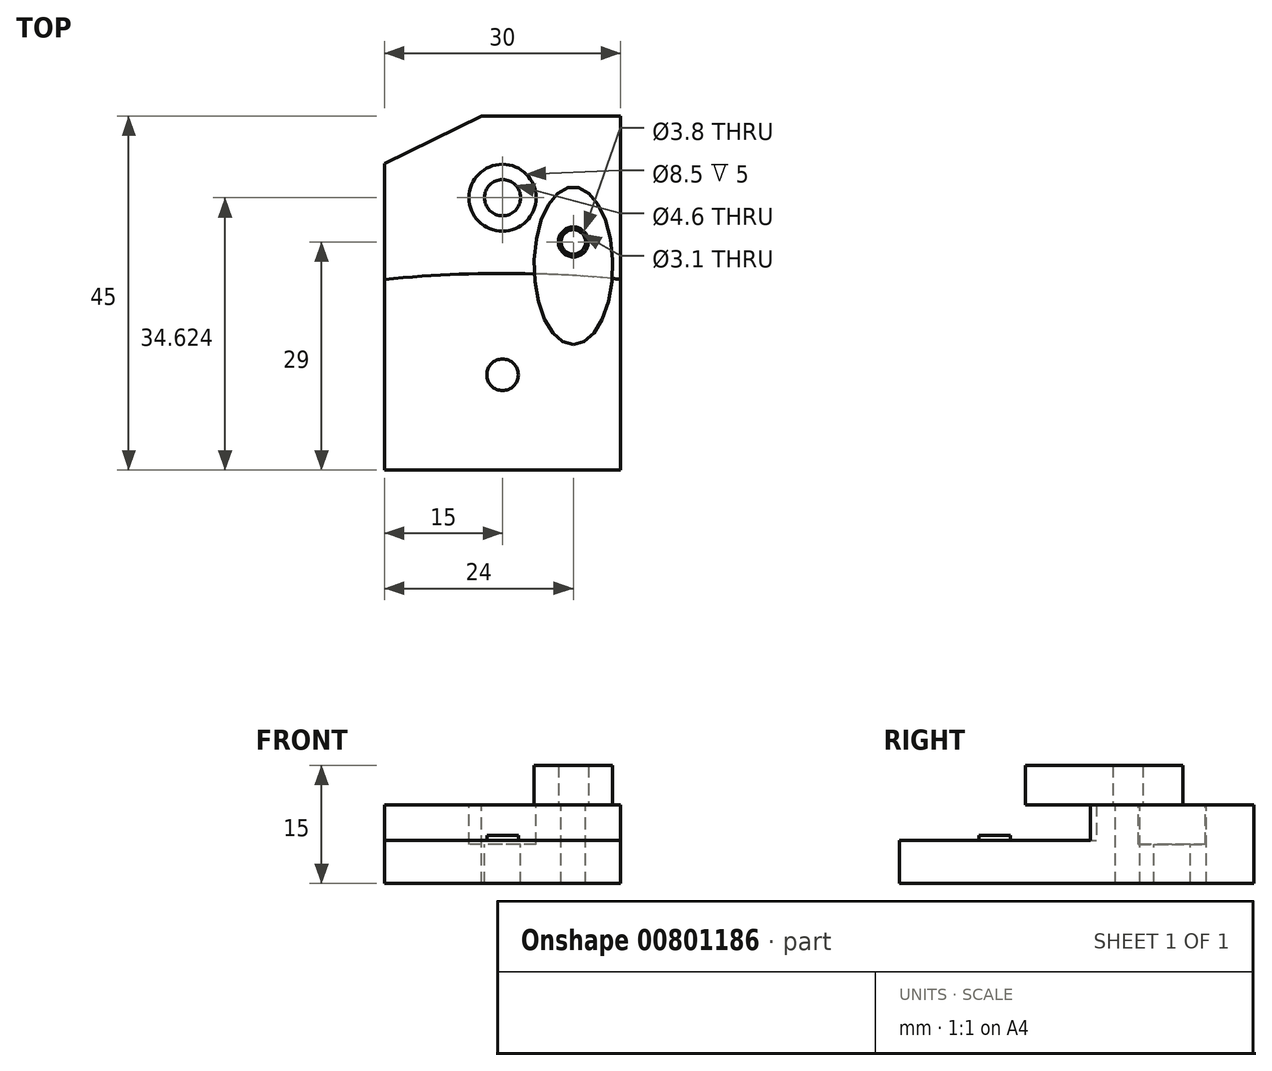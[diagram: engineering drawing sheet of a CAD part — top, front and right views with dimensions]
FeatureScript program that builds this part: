
annotation { "Feature Type Name" : "Feature", "Feature Type Description" : "" }
export const myFeature = defineFeature(function(context is Context, id is Id, definition is map)
    precondition{}
    {
        {
            var Q0;
            Q0=qCreatedBy(makeId("Top.planeOp"),FACE);
            var sketch = newSketch(context, id + "F0", { "sketchPlane" : qUnion([Q0])});
            skLineSegment(sketch, "E0.bottom", {"start": v(15, 22.5) * mm, "end": v(-15, 22.5) * mm});
            skLineSegment(sketch, "E0.top", {"start": v(15, -22.5) * mm, "end": v(-15, -22.5) * mm});
            skLineSegment(sketch, "E0.left", {"start": v(15, 22.5) * mm, "end": v(15, -22.5) * mm});
            skLineSegment(sketch, "E0.right", {"start": v(-15, 22.5) * mm, "end": v(-15, -22.5) * mm});
            skPoint(sketch, "E0.middle", {"position": v(0, 0) * mm});
            skLineSegment(sketch, "E1", {"start": v(15, 2.5) * mm, "end": v(-15, 2.5) * mm});
            skSolve(sketch);
        }
        {
            var Q0;
            {var subQ0=sQuery(id+"F0.wireOp",EDGE,"E0.top");Q0=makeQuery(id+"F0.imprint","IMPRINT",FACE,{"disambiguationData":[TD([[makeQuery(id+"F0.imprint","IMPRINT",EDGE,{"derivedFrom":subQ0}),-1.0]])]});}
            extrude(context, id + "F1", {"entities" : qUnion([Q0]), "oppositeDirection" : true, "depth" : 5.5 * mm, "offsetDistance" : 25 * mm});
        }
        {
            var Q0;
            {var subQ0=sQuery(id+"F0.wireOp",EDGE,"E0.bottom");Q0=makeQuery(id+"F0.imprint","IMPRINT",FACE,{"disambiguationData":[TD([[makeQuery(id+"F0.imprint","IMPRINT",EDGE,{"derivedFrom":subQ0}),1.0]])]});}
            extrude(context, id + "F2", {"entities" : qUnion([Q0]), "operationType" : NewBodyOperationType.ADD, "oppositeDirection" : true, "depth" : 5.5 * mm, "offsetDistance" : 25 * mm, "hasSecondDirection" : true, "secondDirectionOppositeDirection" : false, "secondDirectionDepth" : 4.5 * mm});
        }
        {
            var Q0;
            Q0=makeQuery(id+"F1.opExtrude","CAP_FACE",FACE,{"disambiguationData":[OSD([sQuery(id+"F0.wireOp",EDGE,"E0.top"),sQuery(id+"F0.wireOp",EDGE,"E0.left"),sQuery(id+"F0.wireOp",EDGE,"E0.right"),sQuery(id+"F0.wireOp",EDGE,"E1")])],"isStart":true});
            var sketch = newSketch(context, id + "F3", { "sketchPlane" : qUnion([Q0])});
            skLineSegment(sketch, "E2", {"start": v(0, 2.5) * mm, "end": v(0, -147.5) * mm, "construction": true});
            skCircle(sketch, "E3", {"center": v(0, -147.5) * mm, "radius": 150 * mm});
            skLineSegment(sketch, "E4", {"start": v(15, 2.6) * mm, "end": v(15, 1.75) * mm});
            skLineSegment(sketch, "E5", {"start": v(-15, 2.5) * mm, "end": v(-15, 1.75) * mm});
            skLineSegment(sketch, "E6", {"start": v(-15, 2.5) * mm, "end": v(15, 2.5) * mm});
            skSolve(sketch);
        }
        {
            var Q0;
            {var subQ0=sQuery(id+"F3.wireOp",EDGE,"E6");var subQ3=sQuery(id+"F3.wireOp",EDGE,"E4");var subQ5=makeQuery(id+"F3.imprint","INTERSECT",VERTEX,{"derivedFrom":[subQ3,subQ0]});Q0=makeQuery(id+"F3.imprint","IMPRINT",FACE,{"disambiguationData":[TD([[makeQuery(id+"F3.imprint","IMPRINT",EDGE,{"disambiguationData":[TD([[subQ5,-1.0]])],"derivedFrom":subQ0}),1.0]])]});}
            var Q1;
            {var subQ0=sQuery(id+"F3.wireOp",EDGE,"E5");Q1=makeQuery(id+"F3.imprint","IMPRINT",FACE,{"disambiguationData":[TD([[makeQuery(id+"F3.imprint","IMPRINT",EDGE,{"derivedFrom":subQ0}),1.0]])]});}
            var Q2;
            Q2=makeQuery(id+"F2.opExtrude","CAP_FACE",FACE,{"disambiguationData":[OSD([sQuery(id+"F0.wireOp",EDGE,"E0.bottom"),sQuery(id+"F0.wireOp",EDGE,"E0.left"),sQuery(id+"F0.wireOp",EDGE,"E0.right"),sQuery(id+"F0.wireOp",EDGE,"E1")])],"isStart":true});
            extrude(context, id + "F4", {"entities" : qUnion([Q0, Q1]), "operationType" : NewBodyOperationType.ADD, "endBound" : BoundingType.UP_TO_SURFACE, "depth" : 4 * mm, "endBoundEntityFace" : qUnion([Q2]), "offsetDistance" : 25 * mm});
        }
        {
            var Q0;
            Q0=makeQuery(id+"F1.opExtrude","CAP_FACE",FACE,{"disambiguationData":[OSD([sQuery(id+"F0.wireOp",EDGE,"E0.top"),sQuery(id+"F0.wireOp",EDGE,"E0.left"),sQuery(id+"F0.wireOp",EDGE,"E0.right"),sQuery(id+"F0.wireOp",EDGE,"E1")])],"isStart":true});
            var sketch = newSketch(context, id + "F5", { "sketchPlane" : qUnion([Q0])});
            skCircle(sketch, "E7", {"center": v(0, -10.38) * mm, "radius": 2 * mm});
            skPoint(sketch, "E7.centerSnap0", {"position": v(15, -10.38) * mm});
            skPoint(sketch, "E7.centerSnap1", {"position": v(0, -22.5) * mm});
            skSolve(sketch);
        }
        {
            var Q0;
            Q0 = qSketchRegion(id + "F5", true);
            extrude(context, id + "F6", {"entities" : qUnion([Q0]), "operationType" : NewBodyOperationType.ADD, "depth" : 0.6 * mm, "offsetDistance" : 25 * mm});
        }
        {
            var Q0;
            {var subQ0=sQuery(id+"F3.wireOp",EDGE,"E6");var subQ1=sQuery(id+"F3.wireOp",EDGE,"E3");Q0=makeQuery(id+"F4.boolean.opBoolean","MERGE",FACE,{"derivedFrom":[makeQuery(id+"F2.opExtrude","CAP_FACE",FACE,{"disambiguationData":[OSD([sQuery(id+"F0.wireOp",EDGE,"E0.bottom"),sQuery(id+"F0.wireOp",EDGE,"E0.left"),sQuery(id+"F0.wireOp",EDGE,"E0.right"),sQuery(id+"F0.wireOp",EDGE,"E1")])],"isStart":true}),makeQuery(id+"F4.opExtrude","CAP_FACE",FACE,{"disambiguationData":[OSD([subQ1,sQuery(id+"F3.wireOp",EDGE,"E4"),subQ0])],"isStart":false}),makeQuery(id+"F4.opExtrude","CAP_FACE",FACE,{"disambiguationData":[OSD([subQ1,sQuery(id+"F3.wireOp",EDGE,"E5"),subQ0])],"isStart":false})]});}
            var sketch = newSketch(context, id + "F7", { "sketchPlane" : qUnion([Q0])});
            skCircle(sketch, "E8", {"center": v(0, 12.12) * mm, "radius": 4.25 * mm});
            skPoint(sketch, "E8.centerSnap0", {"position": v(-15, 12.12) * mm});
            skPoint(sketch, "E8.centerSnap1", {"position": v(0, 22.5) * mm});
            skSolve(sketch);
        }
        {
            var Q0;
            Q0 = qSketchRegion(id + "F7", true);
            extrude(context, id + "F8", {"entities" : qUnion([Q0]), "operationType" : NewBodyOperationType.REMOVE, "oppositeDirection" : true, "depth" : 5 * mm, "offsetDistance" : 25 * mm});
        }
        {
            var Q0;
            Q0=makeQuery(id+"F8.boolean.opBoolean","COPY",FACE,{"derivedFrom":makeQuery(id+"F8.opExtrude","CAP_FACE",FACE,{"disambiguationData":[OSD([sQuery(id+"F7.wireOp",EDGE,"E8")])],"isStart":false})});
            var sketch = newSketch(context, id + "F9", { "sketchPlane" : qUnion([Q0])});
            skCircle(sketch, "E9", {"center": v(0, 12.12) * mm, "radius": 2.3 * mm});
            skSolve(sketch);
        }
        {
            var Q0;
            Q0 = qSketchRegion(id + "F9", true);
            extrude(context, id + "F10", {"entities" : qUnion([Q0]), "operationType" : NewBodyOperationType.REMOVE, "oppositeDirection" : true, "depth" : 25 * mm, "offsetDistance" : 25 * mm});
        }
        {
            var Q0;
            {var subQ0=sQuery(id+"F0.wireOp",EDGE,"E1");var subQ1=sQuery(id+"F0.wireOp",EDGE,"E0.right");var subQ2=sQuery(id+"F0.wireOp",EDGE,"E0.left");var subQ3=sQuery(id+"F0.wireOp",EDGE,"E0.bottom");Q0=makeQuery(id+"F4.boolean.opBoolean","MERGE",FACE,{"derivedFrom":[makeQuery(id+"F2.opExtrude","CAP_FACE",FACE,{"disambiguationData":[OSD([subQ3,subQ2,subQ1,subQ0])],"isStart":true}),makeQuery(id+"F4.opExtrude","CAP_FACE",FACE,{"disambiguationData":[OSD([subQ3,subQ2,subQ1,subQ0]),OD(0.0)],"isStart":false}),makeQuery(id+"F4.opExtrude","CAP_FACE",FACE,{"disambiguationData":[OSD([subQ3,subQ2,subQ1,subQ0]),OD(1.0)],"isStart":false})]});}
            var sketch = newSketch(context, id + "F11", { "sketchPlane" : qUnion([Q0])});
            skCircle(sketch, "E10", {"center": v(9, 6.5) * mm, "radius": 1.55 * mm});
            skLineSegment(sketch, "E11", {"start": v(0, 22.5) * mm, "end": v(0, 20.57) * mm, "construction": true});
            skSolve(sketch);
        }
        {
            var Q0;
            Q0 = qSketchRegion(id + "F11", true);
            extrude(context, id + "F12", {"entities" : qUnion([Q0]), "operationType" : NewBodyOperationType.REMOVE, "oppositeDirection" : true, "depth" : 25 * mm, "offsetDistance" : 25 * mm});
        }
        {
            var Q0;
            {var subQ0=sQuery(id+"F0.wireOp",EDGE,"E1");var subQ1=sQuery(id+"F0.wireOp",EDGE,"E0.right");var subQ2=sQuery(id+"F0.wireOp",EDGE,"E0.left");var subQ3=sQuery(id+"F0.wireOp",EDGE,"E0.bottom");Q0=makeQuery(id+"F4.boolean.opBoolean","MERGE",FACE,{"derivedFrom":[makeQuery(id+"F2.opExtrude","CAP_FACE",FACE,{"disambiguationData":[OSD([subQ3,subQ2,subQ1,subQ0])],"isStart":true}),makeQuery(id+"F4.opExtrude","CAP_FACE",FACE,{"disambiguationData":[OSD([subQ3,subQ2,subQ1,subQ0]),OD(0.0)],"isStart":false}),makeQuery(id+"F4.opExtrude","CAP_FACE",FACE,{"disambiguationData":[OSD([subQ3,subQ2,subQ1,subQ0]),OD(1.0)],"isStart":false})]});}
            var sketch = newSketch(context, id + "F13", { "sketchPlane" : qUnion([Q0])});
            skLineSegment(sketch, "E12", {"start": v(-2.66, 22.5) * mm, "end": v(-15, 16.48) * mm});
            skLineSegment(sketch, "E13", {"start": v(-15, 16.48) * mm, "end": v(-15, 22.5) * mm});
            skLineSegment(sketch, "E14", {"start": v(-15, 22.5) * mm, "end": v(-2.66, 22.5) * mm});
            skSolve(sketch);
        }
        {
            var Q0;
            Q0 = qSketchRegion(id + "F13", true);
            extrude(context, id + "F14", {"entities" : qUnion([Q0]), "operationType" : NewBodyOperationType.REMOVE, "oppositeDirection" : true, "depth" : 25 * mm, "offsetDistance" : 25 * mm});
        }
        {
            var Q0;
            {var subQ0=sQuery(id+"F0.wireOp",EDGE,"E1");var subQ1=sQuery(id+"F0.wireOp",EDGE,"E0.right");var subQ2=sQuery(id+"F0.wireOp",EDGE,"E0.left");var subQ3=sQuery(id+"F0.wireOp",EDGE,"E0.bottom");Q0=makeQuery(id+"F4.boolean.opBoolean","MERGE",FACE,{"derivedFrom":[makeQuery(id+"F2.opExtrude","CAP_FACE",FACE,{"disambiguationData":[OSD([subQ3,subQ2,subQ1,subQ0])],"isStart":true}),makeQuery(id+"F4.opExtrude","CAP_FACE",FACE,{"disambiguationData":[OSD([subQ3,subQ2,subQ1,subQ0]),OD(0.0)],"isStart":false}),makeQuery(id+"F4.opExtrude","CAP_FACE",FACE,{"disambiguationData":[OSD([subQ3,subQ2,subQ1,subQ0]),OD(1.0)],"isStart":false})]});}
            var sketch = newSketch(context, id + "F15", { "sketchPlane" : qUnion([Q0])});
            skEllipse(sketch, "E15", {"center": v(9, 3.5) * mm, "majorRadius": 10 * mm, "minorRadius": 5 * mm, "majorAxis": v(0, -1)});
            skCircle(sketch, "E16", {"center": v(9, 6.5) * mm, "radius": 1.9 * mm});
            skPoint(sketch, "E16.centerSnap0", {"position": v(9, 13.5) * mm});
            skSolve(sketch);
        }
        {
            var Q0;
            Q0 = qSketchRegion(id + "F15", true);
            extrude(context, id + "F16", {"entities" : qUnion([Q0]), "depth" : 5 * mm, "offsetDistance" : 25 * mm});
        }
    });
